# Revit family: 200401001_Sanitario Aquapro Al Bco
name_source: partatom
category: Plumbing Fixtures
units: mm (PartAtom-declared; Revit-internal decimal feet)

## family parameters
Always vertical = Yes
Cut with Voids When Loaded = No
OmniClass Number = 23.31.19.17
OmniClass Title = Toilets With Tank
Part Type = Normal
Room Calculation Point = No
Round Connector Dimension = Use Diameter
Shared = No
Work Plane-Based = No

## types (1)
- 200401001_Sanitario Aquapro Al Bco
    Alto = 785 mm  [stored 2.57546 ft]
    Altura de Sello = 65 mm. - 2,55 pulg.
    Ancho = 378 mm
    Creado por = IDD
    Description = Consumo de agua promedio de 3.8 Lpf. (4.8 Lpf. para sólidos / 3.2 Lpf. para líquidos).
    Dimensiones generales producto (H * W * D) = 785 x 714 x 378 mm.
    Espejo de Agua = 162 x 235 mm. - 6 3/8 x 9 1/4 pulg.
    Fecha de creación = 13/08/2020
    Manufacturer = CORONA
    Material = Corona_Porcelana_Sanitaria
    Material 2 = Corona_Aluminio
    Model = Sanitario Aquapro Al Bco
    Peso Neto aprox = Taza: 23,38 kg. - 51,55 lbs.Tanque: 9,98 kg. - 22,00 lbs.
    Presion maxima = 20 - 80 PSI
    Profundidad = 714 mm
    Sistema de Carga = Por gravedad
    URL = https://corona.co

note: [stored X ft] marks values corroborated as IEEE doubles in the binary element streams (Revit-internal decimal feet)

## geometry (parser evidence)
native form markers: Sweep x2
no freeform markers — native parametric forms only
